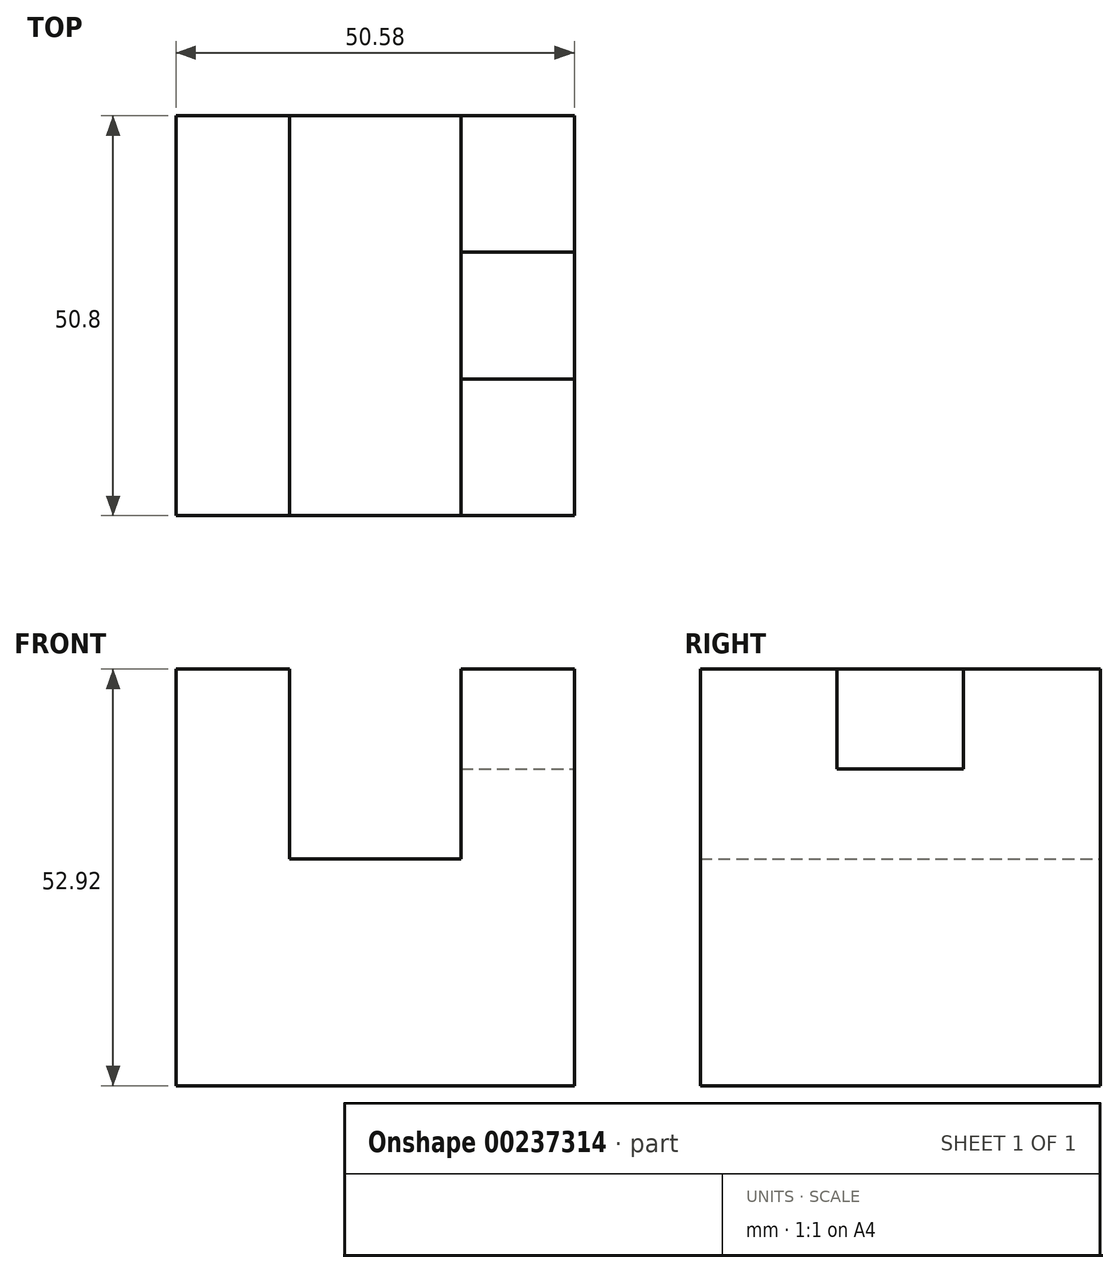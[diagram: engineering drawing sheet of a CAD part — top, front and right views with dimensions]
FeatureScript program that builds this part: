
annotation { "Feature Type Name" : "Feature", "Feature Type Description" : "" }
export const myFeature = defineFeature(function(context is Context, id is Id, definition is map)
    precondition{}
    {
        {
            var Q0;
            Q0=qCreatedBy(makeId("Front.planeOp"),FACE);
            var sketch = newSketch(context, id + "F0", { "sketchPlane" : qUnion([Q0])});
            skLineSegment(sketch, "E0.bottom", {"start": v(-25.3, 26.46) * mm, "end": v(25.3, 26.46) * mm});
            skLineSegment(sketch, "E0.top", {"start": v(-25.3, -26.46) * mm, "end": v(25.3, -26.46) * mm});
            skLineSegment(sketch, "E0.left", {"start": v(-25.3, 26.46) * mm, "end": v(-25.3, -26.46) * mm});
            skLineSegment(sketch, "E0.right", {"start": v(25.3, 26.46) * mm, "end": v(25.3, -26.46) * mm});
            skPoint(sketch, "E0.middle", {"position": v(0, 0) * mm});
            skLineSegment(sketch, "E1.bottom", {"start": v(10.9, 50.59) * mm, "end": v(-10.9, 50.59) * mm});
            skLineSegment(sketch, "E1.top", {"start": v(10.9, 2.33) * mm, "end": v(-10.9, 2.33) * mm});
            skLineSegment(sketch, "E1.left", {"start": v(10.9, 50.59) * mm, "end": v(10.9, 2.33) * mm});
            skLineSegment(sketch, "E1.right", {"start": v(-10.9, 50.59) * mm, "end": v(-10.9, 2.33) * mm});
            skPoint(sketch, "E1.middle", {"position": v(0, 26.46) * mm});
            skSolve(sketch);
        }
        {
            var Q0;
            Q0=makeQuery(id+"F0.imprint","IMPRINT",FACE,{"disambiguationData":[TD([[makeQuery(id+"F0.imprint","IMPRINT",EDGE,{"derivedFrom":sQuery(id+"F0.wireOp",EDGE,"E0.top")}),1.0]])]});
            extrude(context, id + "F1", {"entities" : qUnion([Q0]), "depth" : 25.4 * mm, "hasSecondDirection" : true, "secondDirectionOppositeDirection" : true, "secondDirectionDepth" : 25.4 * mm});
        }
        {
            var Q0;
            {var subQ0=sQuery(id+"F0.wireOp",EDGE,"E0.bottom");Q0=makeQuery(id+"F1.opExtrude","SWEPT_FACE",FACE,{"disambiguationData":[OSD([subQ0]),TDD([makeQuery(id+"F0.imprint","IMPRINT",EDGE,{"disambiguationData":[TD([[makeQuery(id+"F0.imprint","INTERSECT",VERTEX,{"derivedFrom":[subQ0,sQuery(id+"F0.wireOp",EDGE,"E0.right")]}),1.0]])],"derivedFrom":subQ0})])]});}
            var sketch = newSketch(context, id + "F2", { "sketchPlane" : qUnion([Q0])});
            skLineSegment(sketch, "E2.bottom", {"start": v(10.9, 8.04) * mm, "end": v(25.3, 8.04) * mm});
            skLineSegment(sketch, "E2.top", {"start": v(10.9, -8.04) * mm, "end": v(25.3, -8.04) * mm});
            skLineSegment(sketch, "E2.left", {"start": v(10.9, 8.04) * mm, "end": v(10.9, -8.04) * mm});
            skLineSegment(sketch, "E2.right", {"start": v(25.3, 8.04) * mm, "end": v(25.3, -8.04) * mm});
            skPoint(sketch, "E2.middle", {"position": v(18.1, 0) * mm});
            skPoint(sketch, "E2.middle.positionSnap0", {"position": v(10.9, 0) * mm});
            skPoint(sketch, "E2.middle.positionSnap1", {"position": v(18.1, 25.4) * mm});
            skPoint(sketch, "E2.centerSnap0", {"position": v(10.9, 0) * mm});
            skPoint(sketch, "E2.centerSnap1", {"position": v(18.1, 25.4) * mm});
            skSolve(sketch);
        }
        {
            var Q0;
            Q0=makeQuery(id+"F2.imprint","IMPRINT",FACE,{"disambiguationData":[TD([[makeQuery(id+"F2.imprint","IMPRINT",EDGE,{"derivedFrom":sQuery(id+"F2.wireOp",EDGE,"E2.bottom")}),-1.0]])]});
            extrude(context, id + "F3", {"entities" : qUnion([Q0]), "operationType" : NewBodyOperationType.REMOVE, "oppositeDirection" : true, "depth" : 12.7 * mm});
        }
    });
